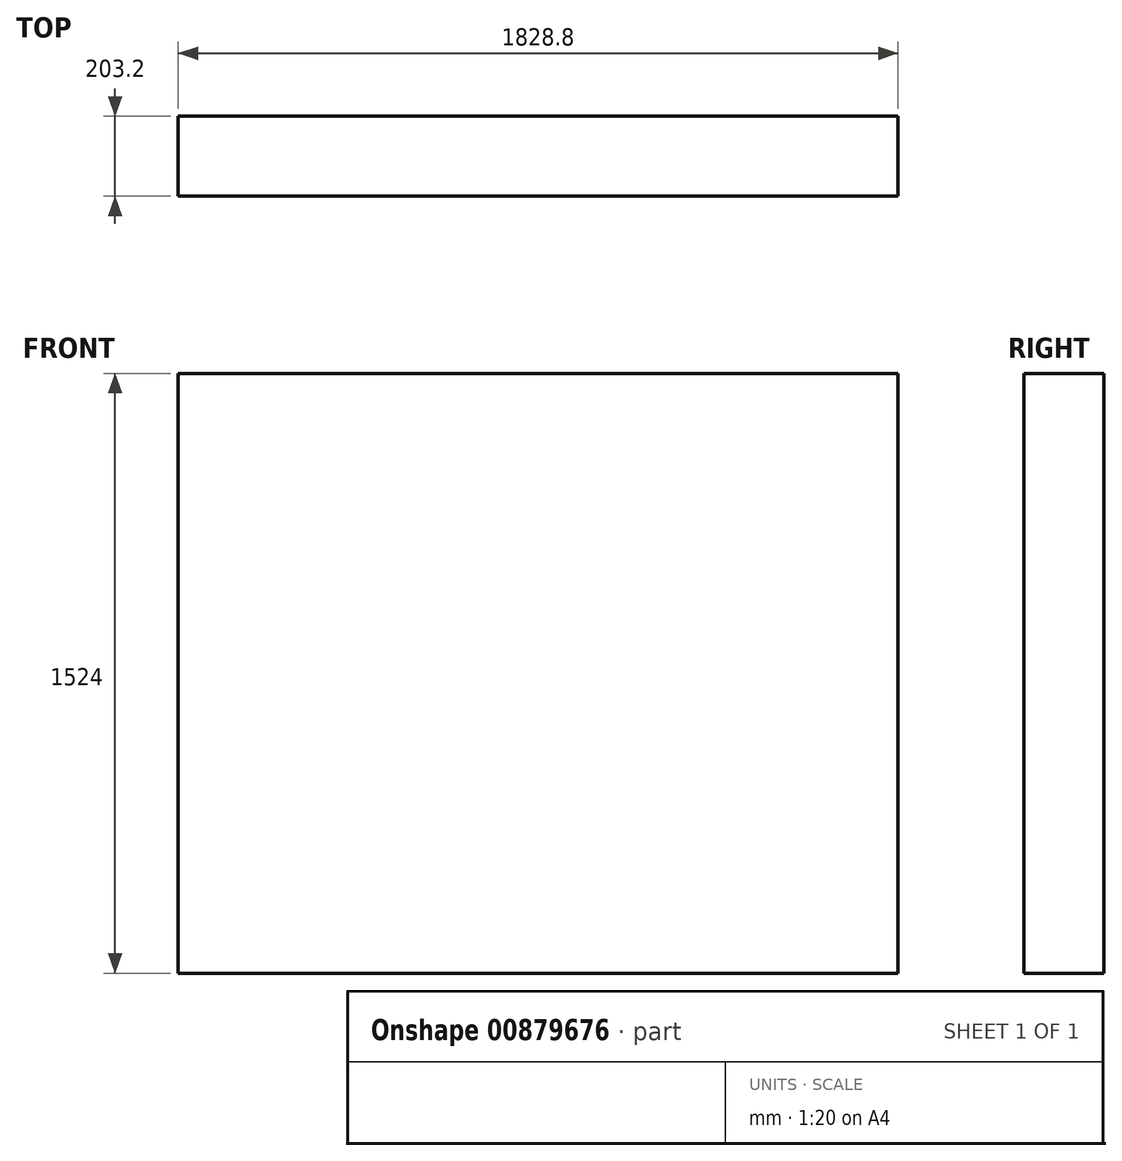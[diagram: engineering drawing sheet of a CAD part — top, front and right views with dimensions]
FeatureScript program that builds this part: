
annotation { "Feature Type Name" : "Feature", "Feature Type Description" : "" }
export const myFeature = defineFeature(function(context is Context, id is Id, definition is map)
    precondition{}
    {
        {
            var Q0;
            Q0=qCreatedBy(makeId("Front.planeOp"),FACE);
            var sketch = newSketch(context, id + "F0", { "sketchPlane" : qUnion([Q0])});
            skLineSegment(sketch, "E0.bottom", {"start": v(-913.05, 835.65) * mm, "end": v(915.75, 835.65) * mm});
            skLineSegment(sketch, "E0.top", {"start": v(-913.05, -688.35) * mm, "end": v(915.75, -688.35) * mm});
            skLineSegment(sketch, "E0.left", {"start": v(-913.05, 835.65) * mm, "end": v(-913.05, -688.35) * mm});
            skLineSegment(sketch, "E0.right", {"start": v(915.75, 835.65) * mm, "end": v(915.75, -688.35) * mm});
            skSolve(sketch);
        }
        {
            var Q0;
            Q0=makeQuery(id+"F0.imprint","IMPRINT",FACE,{"disambiguationData":[TD([[makeQuery(id+"F0.imprint","IMPRINT",EDGE,{"derivedFrom":sQuery(id+"F0.wireOp",EDGE,"E0.bottom")}),-1.0]])]});
            extrude(context, id + "F1", {"entities" : qUnion([Q0]), "depth" : 203.2 * mm, "offsetDistance" : 25.4 * mm});
        }
    });
